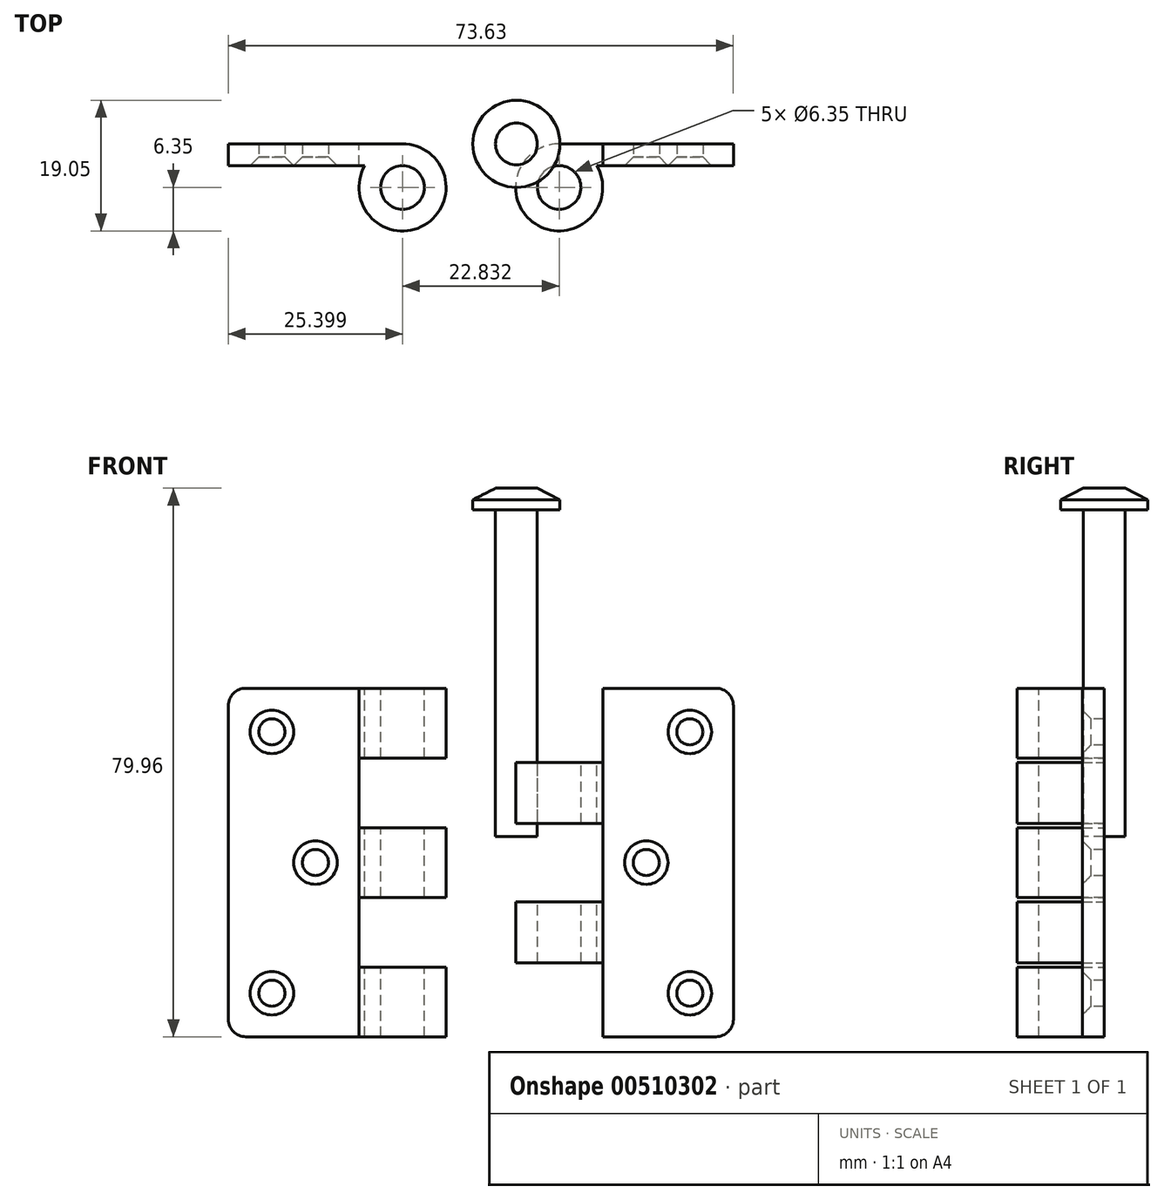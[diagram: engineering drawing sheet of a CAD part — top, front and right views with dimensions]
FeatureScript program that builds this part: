
annotation { "Feature Type Name" : "Feature", "Feature Type Description" : "" }
export const myFeature = defineFeature(function(context is Context, id is Id, definition is map)
    precondition{}
    {
        {
            var Q0;
            Q0=qCreatedBy(makeId("Front.planeOp"),FACE);
            var sketch = newSketch(context, id + "F0", { "sketchPlane" : qUnion([Q0])});
            skLineSegment(sketch, "E0.bottom", {"start": v(-44.61, 38.03) * mm, "end": v(-19.21, 38.03) * mm});
            skLineSegment(sketch, "E0.top", {"start": v(-44.61, -12.77) * mm, "end": v(-19.21, -12.77) * mm});
            skLineSegment(sketch, "E0.left", {"start": v(-44.61, 38.03) * mm, "end": v(-44.61, -12.77) * mm});
            skLineSegment(sketch, "E0.right", {"start": v(-19.21, 38.03) * mm, "end": v(-19.21, -12.77) * mm});
            skSolve(sketch);
        }
        {
            var Q0;
            Q0=qSketchRegion(id+"F0",true);
            extrude(context, id + "F1", {"entities" : qUnion([Q0]), "depth" : 3.17 * mm});
        }
        {
            var Q0;
            Q0=makeQuery(id+"F1.opExtrude","SWEPT_FACE",FACE,{"disambiguationData":[OSD([sQuery(id+"F0.wireOp",EDGE,"E0.bottom")])]});
            var sketch = newSketch(context, id + "F2", { "sketchPlane" : qUnion([Q0])});
            skCircle(sketch, "E1", {"center": v(-19.21, -6.35) * mm, "radius": 6.35 * mm});
            skCircle(sketch, "E2", {"center": v(-19.21, -6.35) * mm, "radius": 3.18 * mm});
            skSolve(sketch);
        }
        {
            var Q0;
            {var subQ5=sQuery(id+"F2.wireOp",EDGE,"E2");Q0=makeQuery(id+"F2.imprint","IMPRINT",FACE,{"disambiguationData":[TD([[makeQuery(id+"F2.imprint","IMPRINT",EDGE,{"derivedFrom":subQ5}),-1.0]])]});}
            var Q1;
            {var subQ1=sQuery(id+"F0.wireOp",EDGE,"E0.bottom");var subQ2=makeQuery(id+"F1.opExtrude","SWEPT_EDGE",EDGE,{"disambiguationData":[OSD([subQ1,sQuery(id+"F0.wireOp",EDGE,"E0.right")])]});Q1=makeQuery(id+"F2.imprint","IMPRINT",FACE,{"disambiguationData":[TD([[makeQuery(id+"F2.imprint","IMPRINT",EDGE,{"derivedFrom":subQ2}),1.0]])]});}
            var Q2;
            Q2=makeQuery(id+"F1.opExtrude","SWEPT_FACE",FACE,{"disambiguationData":[OSD([sQuery(id+"F0.wireOp",EDGE,"E0.top")])]});
            extrude(context, id + "F3", {"entities" : qUnion([Q0, Q1]), "operationType" : NewBodyOperationType.ADD, "endBound" : BoundingType.UP_TO_SURFACE, "oppositeDirection" : true, "endBoundEntityFace" : qUnion([Q2]), "depth" : 25.4 * mm});
        }
        {
            var Q0;
            Q0=makeQuery(id+"F1.opExtrude","CAP_FACE",FACE,{"disambiguationData":[OSD([sQuery(id+"F0.wireOp",EDGE,"E0.bottom"),sQuery(id+"F0.wireOp",EDGE,"E0.top"),sQuery(id+"F0.wireOp",EDGE,"E0.left"),sQuery(id+"F0.wireOp",EDGE,"E0.right")])],"isStart":false});
            var sketch = newSketch(context, id + "F4", { "sketchPlane" : qUnion([Q0])});
            skLineSegment(sketch, "E3", {"start": v(-34.66, 38.03) * mm, "end": v(-34.66, -12.77) * mm, "construction": true});
            skLineSegment(sketch, "E4", {"start": v(-24.7, 12.63) * mm, "end": v(-44.61, 12.63) * mm, "construction": true});
            skLineSegment(sketch, "E5", {"start": v(-24.7, -6.42) * mm, "end": v(-44.61, -6.42) * mm, "construction": true});
            skLineSegment(sketch, "E6", {"start": v(-24.7, 31.68) * mm, "end": v(-44.61, 31.68) * mm, "construction": true});
            skPoint(sketch, "E7", {"position": v(-38.26, 31.68) * mm});
            skPoint(sketch, "E8", {"position": v(-31.91, 12.63) * mm});
            skPoint(sketch, "E9", {"position": v(-38.26, -6.42) * mm});
            skSolve(sketch);
        }
        {
            var Q0;
            Q0=makeQuery(id+"F1.opExtrude","SWEPT_EDGE",EDGE,{"disambiguationData":[OSD([sQuery(id+"F0.wireOp",EDGE,"E0.bottom"),sQuery(id+"F0.wireOp",EDGE,"E0.left")])]});
            var Q1;
            Q1=makeQuery(id+"F1.opExtrude","SWEPT_EDGE",EDGE,{"disambiguationData":[OSD([sQuery(id+"F0.wireOp",EDGE,"E0.top"),sQuery(id+"F0.wireOp",EDGE,"E0.left")])]});
            fillet(context, id + "F5", {"entities" : qUnion([Q0, Q1]), "radius" : 2.54 * mm, "tangentPropagation" : true, "allowEdgeOverflow" : false});
        }
        {
            var Q0;
            Q0=makeQuery(id+"F0.imprint","IMPRINT",FACE,{"disambiguationData":[TD([[makeQuery(id+"F0.imprint","IMPRINT",EDGE,{"derivedFrom":sQuery(id+"F0.wireOp",EDGE,"E0.bottom")}),-1.0]])]});
            var sketch = newSketch(context, id + "F6", { "sketchPlane" : qUnion([Q0])});
            skLineSegment(sketch, "E10", {"start": v(-25.56, -2.61) * mm, "end": v(-12.86, -2.61) * mm});
            skLineSegment(sketch, "E11", {"start": v(-12.86, -2.61) * mm, "end": v(-12.86, 7.55) * mm});
            skLineSegment(sketch, "E12", {"start": v(-12.86, 7.55) * mm, "end": v(-25.56, 7.55) * mm});
            skLineSegment(sketch, "E13", {"start": v(-25.56, 7.55) * mm, "end": v(-25.56, -2.61) * mm});
            skLineSegment(sketch, "E14", {"start": v(-25.56, 17.7) * mm, "end": v(-12.86, 17.7) * mm});
            skLineSegment(sketch, "E15", {"start": v(-12.86, 17.7) * mm, "end": v(-12.86, 27.87) * mm});
            skLineSegment(sketch, "E16", {"start": v(-12.86, 27.87) * mm, "end": v(-25.56, 27.87) * mm});
            skLineSegment(sketch, "E17", {"start": v(-25.56, 27.87) * mm, "end": v(-25.56, 17.7) * mm});
            skPoint(sketch, "E18", {"position": v(-19.21, -2.61) * mm});
            skLineSegment(sketch, "E19", {"start": v(-19.21, 27.87) * mm, "end": v(-19.21, 38.03) * mm});
            skLineSegment(sketch, "E20", {"start": v(-19.21, 17.7) * mm, "end": v(-19.21, 7.55) * mm});
            skLineSegment(sketch, "E21", {"start": v(-19.21, -2.61) * mm, "end": v(-19.21, -12.77) * mm});
            skLineSegment(sketch, "E22", {"start": v(-12.86, 17.7) * mm, "end": v(-12.86, 7.55) * mm});
            skLineSegment(sketch, "E23", {"start": v(-25.56, 7.55) * mm, "end": v(-25.56, 17.7) * mm});
            skLineSegment(sketch, "E24", {"start": v(-25.56, 27.87) * mm, "end": v(-25.56, 38.04) * mm});
            skLineSegment(sketch, "E25", {"start": v(-25.56, 38.04) * mm, "end": v(-12.86, 38.03) * mm});
            skLineSegment(sketch, "E26", {"start": v(-12.86, 38.03) * mm, "end": v(-12.86, 27.87) * mm});
            skLineSegment(sketch, "E27", {"start": v(-12.86, -2.61) * mm, "end": v(-12.86, -12.77) * mm});
            skLineSegment(sketch, "E28", {"start": v(-12.86, -12.77) * mm, "end": v(-25.56, -12.77) * mm});
            skLineSegment(sketch, "E29", {"start": v(-25.56, -12.77) * mm, "end": v(-25.56, -2.61) * mm});
            skSolve(sketch);
        }
        {
            var Q0;
            {var subQ0=sQuery(id+"F6.wireOp",EDGE,"E17");Q0=makeQuery(id+"F6.imprint","IMPRINT",FACE,{"disambiguationData":[TD([[makeQuery(id+"F6.imprint","IMPRINT",EDGE,{"derivedFrom":subQ0}),1.0]])]});}
            var Q1;
            {var subQ0=sQuery(id+"F6.wireOp",EDGE,"E15");Q1=makeQuery(id+"F6.imprint","IMPRINT",FACE,{"disambiguationData":[TD([[makeQuery(id+"F6.imprint","IMPRINT",EDGE,{"derivedFrom":subQ0}),1.0]])]});}
            var Q2;
            {var subQ0=sQuery(id+"F6.wireOp",EDGE,"E13");Q2=makeQuery(id+"F6.imprint","IMPRINT",FACE,{"disambiguationData":[TD([[makeQuery(id+"F6.imprint","IMPRINT",EDGE,{"derivedFrom":subQ0}),1.0]])]});}
            var Q3;
            {var subQ0=sQuery(id+"F6.wireOp",EDGE,"E11");Q3=makeQuery(id+"F6.imprint","IMPRINT",FACE,{"disambiguationData":[TD([[makeQuery(id+"F6.imprint","IMPRINT",EDGE,{"derivedFrom":subQ0}),1.0]])]});}
            extrude(context, id + "F7", {"entities" : qUnion([Q0, Q1, Q2, Q3]), "operationType" : NewBodyOperationType.REMOVE, "depth" : 25.4 * mm});
        }
        {
            var Q0;
            Q0=qCreatedBy(makeId("Front.planeOp"),FACE);
            var sketch = newSketch(context, id + "F8", { "sketchPlane" : qUnion([Q0])});
            skLineSegment(sketch, "E30.bottom", {"start": v(3.62, 38.03) * mm, "end": v(29.02, 38.03) * mm});
            skLineSegment(sketch, "E30.top", {"start": v(3.62, -12.77) * mm, "end": v(29.02, -12.77) * mm});
            skLineSegment(sketch, "E30.left", {"start": v(3.62, 38.03) * mm, "end": v(3.62, -12.77) * mm});
            skLineSegment(sketch, "E30.right", {"start": v(29.02, 38.03) * mm, "end": v(29.02, -12.77) * mm});
            skSolve(sketch);
        }
        {
            var Q0;
            Q0=qSketchRegion(id+"F8",true);
            extrude(context, id + "F9", {"entities" : qUnion([Q0]), "depth" : 3.17 * mm});
        }
        {
            var Q0;
            Q0=makeQuery(id+"F9.opExtrude","SWEPT_FACE",FACE,{"disambiguationData":[OSD([sQuery(id+"F8.wireOp",EDGE,"E30.bottom")])]});
            var sketch = newSketch(context, id + "F10", { "sketchPlane" : qUnion([Q0])});
            skCircle(sketch, "E31", {"center": v(3.62, -6.35) * mm, "radius": 6.35 * mm});
            skLineSegment(sketch, "E32", {"start": v(-33.9, -6.35) * mm, "end": v(23.07, -6.35) * mm, "construction": true});
            skCircle(sketch, "E33", {"center": v(3.62, -6.35) * mm, "radius": 3.18 * mm});
            skSolve(sketch);
        }
        {
            var Q0;
            {var subQ5=sQuery(id+"F10.wireOp",EDGE,"E33");Q0=makeQuery(id+"F10.imprint","IMPRINT",FACE,{"disambiguationData":[TD([[makeQuery(id+"F10.imprint","IMPRINT",EDGE,{"derivedFrom":subQ5}),-1.0]])]});}
            var Q1;
            {var subQ1=sQuery(id+"F8.wireOp",EDGE,"E30.bottom");var subQ2=makeQuery(id+"F9.opExtrude","SWEPT_EDGE",EDGE,{"disambiguationData":[OSD([subQ1,sQuery(id+"F8.wireOp",EDGE,"E30.left")])]});Q1=makeQuery(id+"F10.imprint","IMPRINT",FACE,{"disambiguationData":[TD([[makeQuery(id+"F10.imprint","IMPRINT",EDGE,{"derivedFrom":subQ2}),-1.0]])]});}
            var Q2;
            Q2=makeQuery(id+"F9.opExtrude","SWEPT_FACE",FACE,{"disambiguationData":[OSD([sQuery(id+"F8.wireOp",EDGE,"E30.top")])]});
            extrude(context, id + "F11", {"entities" : qUnion([Q0, Q1]), "operationType" : NewBodyOperationType.ADD, "endBound" : BoundingType.UP_TO_SURFACE, "oppositeDirection" : true, "endBoundEntityFace" : qUnion([Q2]), "depth" : 25.4 * mm});
        }
        {
            var Q0;
            Q0=makeQuery(id+"F9.opExtrude","CAP_FACE",FACE,{"disambiguationData":[OSD([sQuery(id+"F8.wireOp",EDGE,"E30.bottom"),sQuery(id+"F8.wireOp",EDGE,"E30.top"),sQuery(id+"F8.wireOp",EDGE,"E30.left"),sQuery(id+"F8.wireOp",EDGE,"E30.right")])],"isStart":true});
            var sketch = newSketch(context, id + "F12", { "sketchPlane" : qUnion([Q0])});
            skLineSegment(sketch, "E34", {"start": v(-9.97, 27.23) * mm, "end": v(2.73, 27.23) * mm});
            skLineSegment(sketch, "E35", {"start": v(2.73, 27.23) * mm, "end": v(2.73, 38.03) * mm});
            skLineSegment(sketch, "E36", {"start": v(2.73, 38.03) * mm, "end": v(-9.97, 38.03) * mm});
            skLineSegment(sketch, "E37", {"start": v(-9.97, 27.23) * mm, "end": v(-9.97, 38.03) * mm});
            skLineSegment(sketch, "E38", {"start": v(-9.97, 27.23) * mm, "end": v(-9.97, -12.77) * mm});
            skLineSegment(sketch, "E39", {"start": v(-9.97, -12.77) * mm, "end": v(2.73, -12.77) * mm});
            skLineSegment(sketch, "E40", {"start": v(2.73, -12.77) * mm, "end": v(2.73, 27.23) * mm});
            skLineSegment(sketch, "E41", {"start": v(2.73, 18.34) * mm, "end": v(-9.97, 18.34) * mm});
            skLineSegment(sketch, "E42", {"start": v(-9.97, 6.91) * mm, "end": v(2.73, 6.91) * mm});
            skLineSegment(sketch, "E43", {"start": v(-9.97, -1.98) * mm, "end": v(2.73, -1.98) * mm});
            skSolve(sketch);
        }
        {
            var Q0;
            {var subQ0=sQuery(id+"F12.wireOp",EDGE,"E35");Q0=makeQuery(id+"F12.imprint","IMPRINT",FACE,{"disambiguationData":[TD([[makeQuery(id+"F12.imprint","IMPRINT",EDGE,{"derivedFrom":subQ0}),1.0]])]});}
            var Q1;
            {var subQ0=sQuery(id+"F12.wireOp",EDGE,"E37");Q1=makeQuery(id+"F12.imprint","IMPRINT",FACE,{"disambiguationData":[TD([[makeQuery(id+"F12.imprint","IMPRINT",EDGE,{"derivedFrom":subQ0}),-1.0]])]});}
            var Q2;
            {var subQ0=sQuery(id+"F12.wireOp",EDGE,"E41");var subQ1=sQuery(id+"F12.wireOp",EDGE,"E38");var subQ2=makeQuery(id+"F12.imprint","INTERSECT",VERTEX,{"derivedFrom":[subQ1,subQ0]});Q2=makeQuery(id+"F12.imprint","IMPRINT",FACE,{"disambiguationData":[TD([[makeQuery(id+"F12.imprint","IMPRINT",EDGE,{"disambiguationData":[TD([[subQ2,-1.0]])],"derivedFrom":subQ1}),1.0]])]});}
            var Q3;
            {var subQ0=sQuery(id+"F12.wireOp",EDGE,"E41");var subQ1=sQuery(id+"F12.wireOp",EDGE,"E40");var subQ2=makeQuery(id+"F12.imprint","INTERSECT",VERTEX,{"derivedFrom":[subQ1,subQ0]});Q3=makeQuery(id+"F12.imprint","IMPRINT",FACE,{"disambiguationData":[TD([[makeQuery(id+"F12.imprint","IMPRINT",EDGE,{"disambiguationData":[TD([[subQ2,1.0]])],"derivedFrom":subQ1}),1.0]])]});}
            var Q4;
            {var subQ0=sQuery(id+"F12.wireOp",EDGE,"E39");var subQ3=sQuery(id+"F12.wireOp",EDGE,"E40");var subQ4=makeQuery(id+"F12.imprint","INTERSECT",VERTEX,{"derivedFrom":[subQ0,subQ3]});Q4=makeQuery(id+"F12.imprint","IMPRINT",FACE,{"disambiguationData":[TD([[makeQuery(id+"F12.imprint","IMPRINT",EDGE,{"disambiguationData":[TD([[subQ4,1.0]])],"derivedFrom":subQ0}),1.0]])]});}
            var Q5;
            {var subQ1=sQuery(id+"F12.wireOp",EDGE,"E38");var subQ3=sQuery(id+"F12.wireOp",EDGE,"E43");var subQ4=makeQuery(id+"F12.imprint","INTERSECT",VERTEX,{"derivedFrom":[subQ1,subQ3]});Q5=makeQuery(id+"F12.imprint","IMPRINT",FACE,{"disambiguationData":[TD([[makeQuery(id+"F12.imprint","IMPRINT",EDGE,{"disambiguationData":[TD([[subQ4,-1.0]])],"derivedFrom":subQ3}),-1.0]])]});}
            extrude(context, id + "F13", {"entities" : qUnion([Q0, Q1, Q2, Q3, Q4, Q5]), "operationType" : NewBodyOperationType.REMOVE, "oppositeDirection" : true, "depth" : 25.4 * mm});
        }
        {
            var Q0;
            Q0=qCreatedBy(makeId("Front.planeOp"),FACE);
            var sketch = newSketch(context, id + "F14", { "sketchPlane" : qUnion([Q0])});
            skLineSegment(sketch, "E44", {"start": v(-5.65, 64.02) * mm, "end": v(-5.65, 16.4) * mm});
            skLineSegment(sketch, "E45", {"start": v(-5.65, 16.4) * mm, "end": v(-2.6, 16.4) * mm});
            skLineSegment(sketch, "E46", {"start": v(-2.6, 16.4) * mm, "end": v(-2.6, 67.2) * mm});
            skLineSegment(sketch, "E47", {"start": v(-2.6, 67.2) * mm, "end": v(-5.65, 67.2) * mm});
            skLineSegment(sketch, "E48", {"start": v(-5.65, 67.2) * mm, "end": v(-8.96, 65.52) * mm});
            skLineSegment(sketch, "E49", {"start": v(-8.96, 65.52) * mm, "end": v(-8.96, 64.02) * mm});
            skLineSegment(sketch, "E50", {"start": v(-8.96, 64.02) * mm, "end": v(-5.65, 64.02) * mm});
            skSolve(sketch);
        }
        {
            var Q0;
            Q0=qSketchRegion(id+"F14",true);
            var Q1;
            Q1=sQuery(id+"F14.wireOp",EDGE,"E46");
            revolve(context, id + "F15", {"entities" : qUnion([Q0]), "axis" : qUnion([Q1]), "revolveType" : RevolveType.FULL});
        }
        {
            var Q0;
            Q0=makeQuery(id+"F9.opExtrude","CAP_FACE",FACE,{"disambiguationData":[OSD([sQuery(id+"F8.wireOp",EDGE,"E30.bottom"),sQuery(id+"F8.wireOp",EDGE,"E30.top"),sQuery(id+"F8.wireOp",EDGE,"E30.left"),sQuery(id+"F8.wireOp",EDGE,"E30.right")])],"isStart":false});
            var sketch = newSketch(context, id + "F16", { "sketchPlane" : qUnion([Q0])});
            skLineSegment(sketch, "E51", {"start": v(19.5, 38.03) * mm, "end": v(19.5, -12.77) * mm, "construction": true});
            skLineSegment(sketch, "E52", {"start": v(9.97, 12.63) * mm, "end": v(29.02, 12.63) * mm, "construction": true});
            skPoint(sketch, "E53", {"position": v(16.32, 12.63) * mm});
            skPoint(sketch, "E54", {"position": v(22.67, 31.68) * mm});
            skPoint(sketch, "E55", {"position": v(22.67, -6.42) * mm});
            skSolve(sketch);
        }
        {
            var Q0;
            Q0=sQuery(id+"F4.wireOp",VERTEX,"E7");
            var Q1;
            Q1=sQuery(id+"F4.wireOp",VERTEX,"E8");
            var Q2;
            Q2=sQuery(id+"F4.wireOp",VERTEX,"E9");
            var Q3;
            Q3=makeQuery(id+"F1.opExtrude","SWEPT_BODY",BODY,{"disambiguationData":[OSD([sQuery(id+"F0.wireOp",EDGE,"E0.bottom"),sQuery(id+"F0.wireOp",EDGE,"E0.top"),sQuery(id+"F0.wireOp",EDGE,"E0.left"),sQuery(id+"F0.wireOp",EDGE,"E0.right")])]});
            hole(context, id + "F17", {"style" : HoleStyle.C_SINK, "endStyle" : HoleEndStyle.THROUGH, "holeDiameter" : 3.8 * mm, "cSinkDiameter" : 6.35 * mm, "cSinkAngle" : 90 * degree, "locations" : qUnion([Q0, Q1, Q2]), "scope" : qUnion([Q3]), "tappedDepth" : 12 * mm, "tapClearance" : 3});
        }
        {
            var Q0;
            Q0=sQuery(id+"F16.wireOp",VERTEX,"E54");
            var Q1;
            Q1=sQuery(id+"F16.wireOp",VERTEX,"E53");
            var Q2;
            Q2=sQuery(id+"F16.wireOp",VERTEX,"E55");
            var Q3;
            Q3=makeQuery(id+"F9.opExtrude","SWEPT_BODY",BODY,{"disambiguationData":[OSD([sQuery(id+"F8.wireOp",EDGE,"E30.bottom"),sQuery(id+"F8.wireOp",EDGE,"E30.top"),sQuery(id+"F8.wireOp",EDGE,"E30.left"),sQuery(id+"F8.wireOp",EDGE,"E30.right")])]});
            hole(context, id + "F18", {"style" : HoleStyle.C_SINK, "endStyle" : HoleEndStyle.THROUGH, "holeDiameter" : 3.8 * mm, "cSinkDiameter" : 6.35 * mm, "cSinkAngle" : 90 * degree, "locations" : qUnion([Q0, Q1, Q2]), "scope" : qUnion([Q3]), "isTappedThrough" : true});
        }
        {
            var Q0;
            Q0=makeQuery(id+"F9.opExtrude","SWEPT_EDGE",EDGE,{"disambiguationData":[OSD([sQuery(id+"F8.wireOp",EDGE,"E30.bottom"),sQuery(id+"F8.wireOp",EDGE,"E30.right")])]});
            var Q1;
            Q1=makeQuery(id+"F9.opExtrude","SWEPT_EDGE",EDGE,{"disambiguationData":[OSD([sQuery(id+"F8.wireOp",EDGE,"E30.top"),sQuery(id+"F8.wireOp",EDGE,"E30.right")])]});
            fillet(context, id + "F19", {"entities" : qUnion([Q0, Q1]), "radius" : 2.54 * mm, "tangentPropagation" : true, "allowEdgeOverflow" : false});
        }
    });
